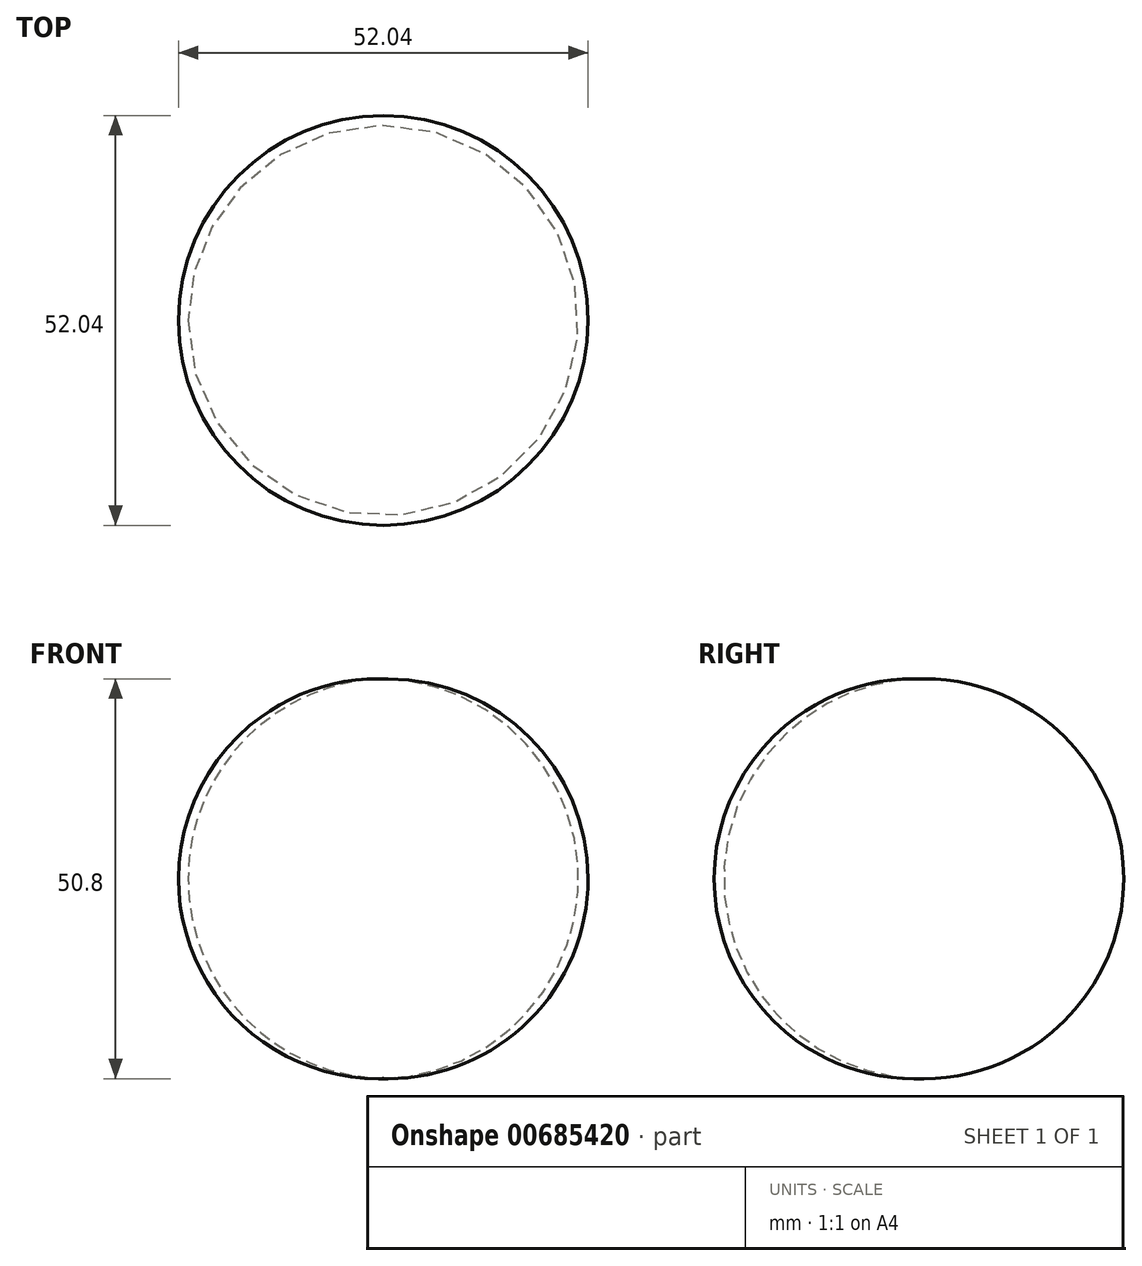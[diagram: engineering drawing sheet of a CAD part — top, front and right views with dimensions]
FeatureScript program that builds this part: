
annotation { "Feature Type Name" : "Feature", "Feature Type Description" : "" }
export const myFeature = defineFeature(function(context is Context, id is Id, definition is map)
    precondition{}
    {
        {
            var Q0;
            Q0=qCreatedBy(makeId("Front.planeOp"),FACE);
            var sketch = newSketch(context, id + "F0", { "sketchPlane" : qUnion([Q0])});
            skArc(sketch, "E0", {"start": v(0, 50.78) * mm, "mid": v(-24.78, 25.4) * mm, "end": v(0, 0) * mm});
            skLineSegment(sketch, "E1", {"start": v(0, 50.78) * mm, "end": v(0, 0) * mm});
            skSolve(sketch);
        }
        {
            var Q0;
            Q0=makeQuery(id+"F0.imprint","IMPRINT",FACE,{"disambiguationData":[TD([[makeQuery(id+"F0.imprint","IMPRINT",EDGE,{"derivedFrom":sQuery(id+"F0.wireOp",EDGE,"E0")}),1.0]])]});
            var Q1;
            Q1=sQuery(id+"F0.wireOp",EDGE,"E1");
            revolve(context, id + "F1", {"entities" : qUnion([Q0]), "axis" : qUnion([Q1]), "revolveType" : RevolveType.FULL});
        }
    });
